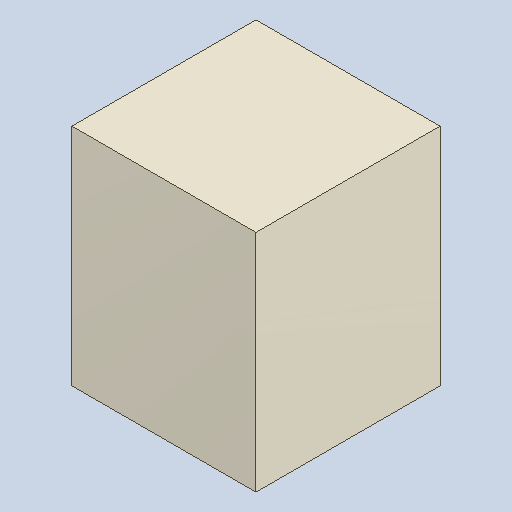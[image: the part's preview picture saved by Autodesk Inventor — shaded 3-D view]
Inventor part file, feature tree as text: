
AUTODESK INVENTOR PART (.ipt)
format: ipt  version: 2023.4 (Build 274418000, 418)  size: 82,944 bytes
history: native  units: mm
features: extrude x1
ambient origin geometry x8: Origin, YZ Plane, XZ Plane, XY Plane, X Axis, Y Axis, Z Axis, Center Point
bodies: Solid1 (feature_tree)
feature tree (1):
  extrude  "Extruded_11"  [1 undecoded]
note: 1 required parameter value undecoded (feature->parameter linkage not recoverable at this tier; creation-order binding heuristic only, values carry confidence <= 0.55)
